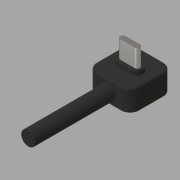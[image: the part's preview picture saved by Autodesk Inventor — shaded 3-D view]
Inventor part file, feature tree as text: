
AUTODESK INVENTOR PART (.ipt)
format: ipt  version: 2019 (Build 230136000, 136)  size: 157,696 bytes
history: native  units: mm
features: extrude x4, sketch x4, fillet x2, other x2, projected_geometry x1
ambient origin geometry x8: Origin, YZ Plane, XZ Plane, XY Plane, X Axis, Y Axis, Z Axis, Center Point
bodies: Solid1 (feature_tree), Solid2 (feature_tree)
feature tree (13):
  extrude  "Extrusion1"  Depth=18.0mm
  fillet  "Fillet1"  Radius=9.0mm
  fillet  "Fillet2"  Radius=0.75mm
  extrude  "Extrusion2"  Depth=5.25mm
  extrude  "Extrusion3"  Depth=5.25mm
  extrude  "Extrusion4"  Depth=33.5mm
  other  "Work Axis1"
  sketch  "Sketch1"  dims[d0=18.0mm d1=18.0mm d2=9.0mm d3=0.0mm d4=0.75mm]
  sketch  "Sketch2"  dims[d5=4.0mm d6=5.25mm]
  sketch  "Sketch3"  dims[d7=10.5mm d8=5.25mm]
  sketch  "Sketch4"  dims[d9=1.75mm d10=0.0mm d11=4.125mm d12=8.25mm d13=2.25mm d14=7.45mm d15=0.0mm d16=6.0mm d17=33.5mm d18=0.0mm]
  projected_geometry  "Projected Loop1"
  other  "Work Point1"
